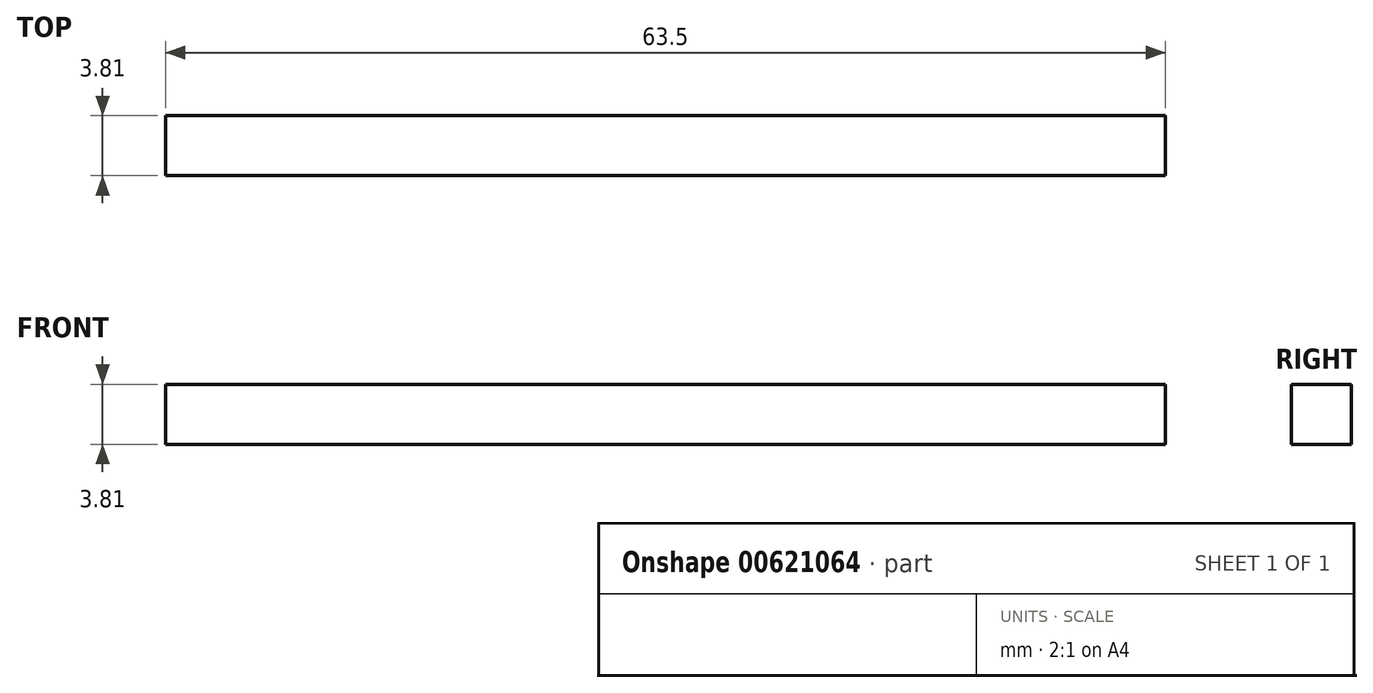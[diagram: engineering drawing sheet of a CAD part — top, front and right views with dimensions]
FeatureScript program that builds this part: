
annotation { "Feature Type Name" : "Feature", "Feature Type Description" : "" }
export const myFeature = defineFeature(function(context is Context, id is Id, definition is map)
    precondition{}
    {
        {
            var Q0;
            Q0=qCreatedBy(makeId("Front.planeOp"),FACE);
            var sketch = newSketch(context, id + "F0", { "sketchPlane" : qUnion([Q0])});
            skLineSegment(sketch, "E0.bottom", {"start": v(0, 0) * mm, "end": v(63.5, 0) * mm});
            skLineSegment(sketch, "E0.top", {"start": v(0, -3.81) * mm, "end": v(63.5, -3.81) * mm});
            skLineSegment(sketch, "E0.left", {"start": v(0, 0) * mm, "end": v(0, -3.81) * mm});
            skLineSegment(sketch, "E0.right", {"start": v(63.5, 0) * mm, "end": v(63.5, -3.81) * mm});
            skSolve(sketch);
        }
        {
            var Q0;
            Q0 = qSketchRegion(id + "F0", true);
            extrude(context, id + "F1", {"entities" : qUnion([Q0]), "depth" : 3.8 * mm, "offsetDistance" : 25.4 * mm});
        }
    });
